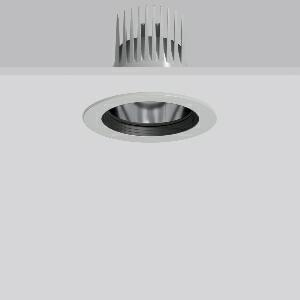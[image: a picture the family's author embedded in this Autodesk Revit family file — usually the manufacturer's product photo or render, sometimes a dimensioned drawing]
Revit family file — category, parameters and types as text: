
# Revit family: heledon_maxi_e_901780_004_76_c2b7
name_source: partatom
category: Lighting Fixtures
units: mm (PartAtom-declared; Revit-internal decimal feet)

## family parameters
Cut with Voids When Loaded = No
Host = Face
Light Source = No
Part Type = Normal
Room Calculation Point = No
Round Connector Dimension = Use Diameter
Shared = No

## types (1)
- HELEDON maxi E (1 x LED Modul 920 meat+, 2150 lm, 2000)
    Apparent Load = 33 VA
    Approval mark = CE
    CIE Flux Codes = 96 100 100 100 100
    Color Rendering = 90
    Color Temperature = 2000
    Default Elevation = 1800 mm
    Description = Series: HELEDON maxi
Round recessed downlight. Housing: die-cast aluminium, powder-coated. Black plastic ring and recessed LED to prevent glare from the side. Optical assembly with reflector made of MIRO-Silver with 98% total light reflection for outstanding efficiency - can be changed without tools. Special LED for illumination of meat included. Suitable for Recessed ceiling mounting. Installation without tools thanks to spring fastening system. Including separate LED converter with connecting cable 600 mm.High quality converter without flickering and stroboscopic effect. Through-wiring box (5 pole) available as accessory. The following accessories can be mounted without use of tools: interchangeable lenses, decorative glasses, honeycomb louvre, clear and frosted diffusers, white interchangeable plastic ring. 
Colour: silver
Diameter: 162 mm
Height: 3 mm
Cut-out diameter: 152 mm
Recess height: 200 mm
Luminaire: recess height: 135 mm
Lamp: LED
Socket: without socket
Colour temperature: meat +
System power: 33 W
Rated luminous flux: 2150 lm
Luminous efficiency: 65 lm/W
Control gear: Converter, dimmable, DALI
Protection class: II
Type of protection: IP 20
    Height = 0 mm  [stored 0 ft]
    Lamp = 1 x LED Modul 920 meat+
    Lamp Light Flux = 2150 lm
    Lamp count = 1
    Length = 162 mm
    Lifetime = 50000 h
    Luminous efficacy = 65 lm/W
    Manufacturer = RZB
    ModVariant = No
    Model = 901780.004.76
    Mounting Place = Ceiling
    Mounting Type = Recessed
    Number of Poles = 1
    OnlyDefault = Yes
    Power Factor = 1
    Product Name = HELEDON maxi E
    Product group = Recessed downlights
    ProductGroupID = 402
    Protection Class = Protection class II
    Protection Degree = IP 20
    RLX_Detail_Level = 1
    RLX_Emergency_Light_Flux = 0 lm
    RLX_Emergency_Type = 0
    RLX_Emergency_Type_DB = No
    RlxData = <blob elided: 119009 chars, md5=c6b959f4>
    Socket = socket
    Standby Power = 0 W
    System Light Flux = 2150 lm
    System Power = 33 W
    Type Comments = Product without accessories
    Type Image = 901662.004.jpg
    URL = http://relux.com
    VarID = ---
    Voltage = 230 V
    Voltage Range = 220-240 V
    Weight = 0.00 kg
    Width = 0 mm  [stored 0 ft]

note: [stored X ft] marks values corroborated as IEEE doubles in the binary element streams (Revit-internal decimal feet)

## geometry (parser evidence)
native form markers: Blend x4, Sweep x10
no freeform markers — native parametric forms only
